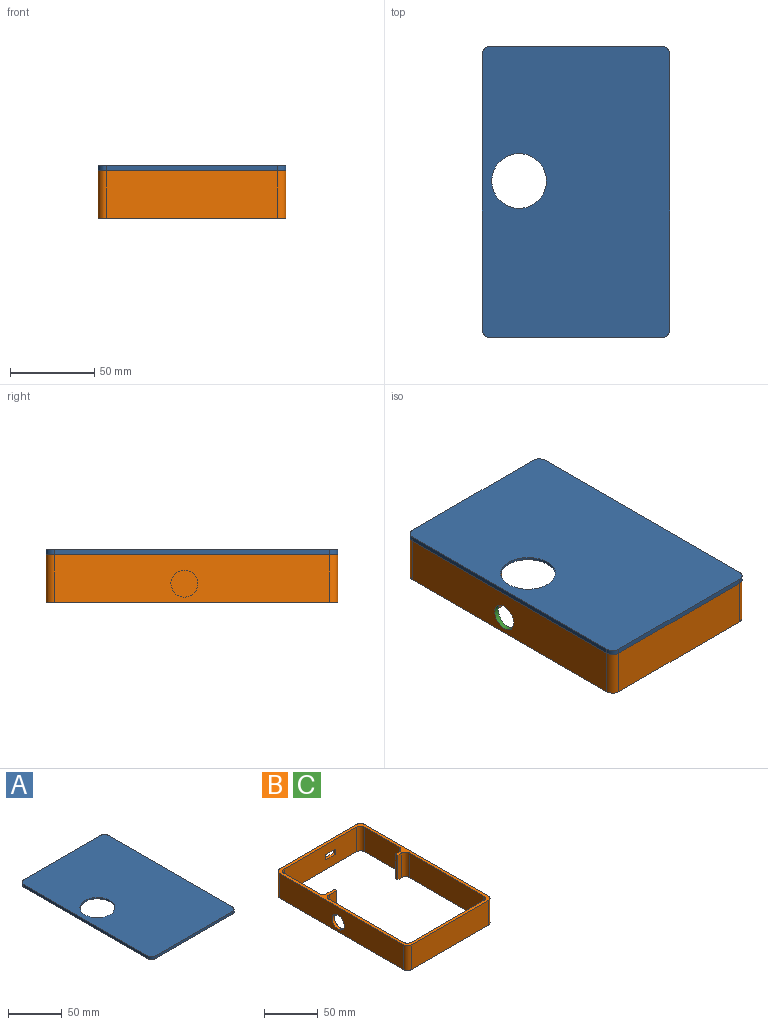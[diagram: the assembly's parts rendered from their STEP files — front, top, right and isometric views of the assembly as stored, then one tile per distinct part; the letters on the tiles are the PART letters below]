
ASSEMBLY  parts=3 mates=1
PART A: 32 faces, bbox 111.5x173x3 mm
  f0: plane 173x111.5mm, normal (0,0,-1), area 1767.5mm2, adj f1,f2,f3,f4,f5,f6,f7,f8
  f1: plane 101.5x3mm, normal (0,1,0), area 304.5mm2, adj f0,f2,f8,f9
  f2: cylinder r=5mm len=5mm, axis (0,0,-1), area 23.6mm2, adj f0,f1,f3,f9
  f3: plane 163x3mm, normal (-1,0,0), area 489mm2, adj f0,f2,f4,f9
  f4: cylinder r=5mm len=5mm, axis (0,0,-1), area 23.6mm2, adj f0,f3,f5,f9
  f5: plane 101.5x3mm, normal (0,-1,0), area 304.5mm2, adj f0,f4,f6,f9
  f6: cylinder r=5mm len=5mm, axis (0,0,-1), area 23.6mm2, adj f0,f5,f7,f9
  f7: plane 163x3mm, normal (1,0,0), area 489mm2, adj f0,f6,f8,f9
  f8: cylinder r=5mm len=5mm, axis (0,0,-1), area 23.6mm2, adj f0,f1,f7,f9
  f9: plane 173x111.5mm, normal (0,0,1), area 18439.7mm2, adj f1,f2,f3,f4,f5,f6,f7,f8
  f10: plane 98x1.5mm, normal (1,0,0), area 147mm2, adj f0,f11,f29,f30
  f11: cylinder r=5mm len=5mm, axis (0,0,-1), area 11.8mm2, adj f0,f10,f12,f30
  f12: plane 95.5x1.5mm, normal (0,1,0), area 143.3mm2, adj f0,f11,f13,f30
  f13: cylinder r=5mm len=5mm, axis (0,0,-1), area 11.8mm2, adj f0,f12,f14,f30
  f14: plane 98x1.5mm, normal (-1,0,0), area 147mm2, adj f0,f13,f15,f30
  f15: cylinder r=5mm len=5mm, axis (0,0,-1), area 11.8mm2, adj f0,f14,f16,f30
  f16: plane 5x1.5mm, normal (0,-1,0), area 7.5mm2, adj f0,f15,f17,f30
  f17: plane 3x1.5mm, normal (-1,0,0), area 4.5mm2, adj f0,f16,f18,f30
  f18: plane 5x1.5mm, normal (0,1,0), area 7.5mm2, adj f0,f17,f19,f30
  f19: cylinder r=5mm len=5mm, axis (0,0,-1), area 11.8mm2, adj f0,f18,f20,f30
  f20: plane 46x1.5mm, normal (-1,0,0), area 69mm2, adj f0,f19,f21,f30
  f21: cylinder r=5mm len=5mm, axis (0,0,-1), area 11.8mm2, adj f0,f20,f22,f30
  f22: plane 95.5x1.5mm, normal (0,-1,0), area 143.3mm2, adj f0,f21,f23,f30
  f23: cylinder r=5mm len=5mm, axis (0,0,-1), area 11.8mm2, adj f0,f22,f24,f30
  f24: plane 46x1.5mm, normal (1,0,0), area 69mm2, adj f0,f23,f25,f30
  f25: cylinder r=5mm len=5mm, axis (0,0,-1), area 11.8mm2, adj f0,f24,f26,f30
  f26: plane 10x1.5mm, normal (0,1,0), area 15mm2, adj f0,f25,f27,f30
  f27: plane 3x1.5mm, normal (1,0,0), area 4.5mm2, adj f0,f26,f28,f30
  f28: plane 10x1.5mm, normal (0,-1,0), area 15mm2, adj f0,f27,f29,f30
  f29: cylinder r=5mm len=5mm, axis (0,0,-1), area 11.8mm2, adj f0,f10,f28,f30
  f30: plane 167x105.5mm, normal (0,0,-1), area 16672.2mm2, adj f10,f11,f12,f13,f14,f15,f16,f17
  f31: cylinder r=16.24mm len=32.48mm, axis (0,0,1), area 153mm2, adj f9,f30
PART B: 35 faces, bbox 111.5x173x28 mm
  f0: plane 101.5x28mm, normal (0,1,0), area 2764mm2, adj f2,f27,f28,f29,f31,f32,f33,f34
  f1: plane 95.5x28mm, normal (0,-1,0), area 2596mm2, adj f19,f20,f28,f29,f31,f32,f33,f34
  f2: cylinder r=5mm len=28mm, axis (0,0,-1), area 219.9mm2, adj f0,f3,f28,f29
  f3: plane 163x28mm, normal (-1,0,0), area 4362.9mm2, adj f2,f4,f28,f29,f30
  f4: cylinder r=5mm len=28mm, axis (0,0,-1), area 219.9mm2, adj f3,f5,f28,f29
  f5: plane 101.5x28mm, normal (0,-1,0), area 2842mm2, adj f4,f6,f28,f29
  f6: cylinder r=5mm len=28mm, axis (0,0,-1), area 219.9mm2, adj f5,f7,f28,f29
  f7: plane 163x28mm, normal (1,0,0), area 4564mm2, adj f6,f27,f28,f29
  f8: plane 98x28mm, normal (-1,0,0), area 2744mm2, adj f9,f26,f28,f29
  f9: cylinder r=5mm len=28mm, axis (0,0,-1), area 219.9mm2, adj f8,f10,f28,f29
  f10: plane 95.5x28mm, normal (0,1,0), area 2674mm2, adj f9,f11,f28,f29
  f11: cylinder r=5mm len=28mm, axis (0,0,-1), area 219.9mm2, adj f10,f12,f28,f29
  f12: plane 98x28mm, normal (1,0,0), area 2542.9mm2, adj f11,f13,f28,f29,f30
  f13: cylinder r=5mm len=28mm, axis (0,0,-1), area 219.9mm2, adj f12,f14,f28,f29
  f14: plane 28x10mm, normal (0,-1,0), area 280mm2, adj f13,f15,f28,f29
  f15: plane 28x3mm, normal (1,0,0), area 84mm2, adj f14,f16,f28,f29
  f16: plane 28x10mm, normal (0,1,0), area 280mm2, adj f15,f17,f28,f29
  f17: cylinder r=5mm len=28mm, axis (0,0,-1), area 219.9mm2, adj f16,f18,f28,f29
  f18: plane 46x28mm, normal (1,0,0), area 1288mm2, adj f17,f19,f28,f29
  f19: cylinder r=5mm len=28mm, axis (0,0,-1), area 219.9mm2, adj f1,f18,f28,f29
  f20: cylinder r=5mm len=28mm, axis (0,0,-1), area 219.9mm2, adj f1,f21,f28,f29
  f21: plane 46x28mm, normal (-1,0,0), area 1288mm2, adj f20,f22,f28,f29
  f22: cylinder r=5mm len=28mm, axis (0,0,-1), area 219.9mm2, adj f21,f23,f28,f29
  f23: plane 28x5mm, normal (0,1,0), area 140mm2, adj f22,f24,f28,f29
  f24: plane 28x3mm, normal (-1,0,0), area 84mm2, adj f23,f25,f28,f29
  f25: plane 28x5mm, normal (0,-1,0), area 140mm2, adj f24,f26,f28,f29
  f26: cylinder r=5mm len=28mm, axis (0,0,-1), area 219.9mm2, adj f8,f25,f28,f29
  f27: cylinder r=5mm len=28mm, axis (0,0,-1), area 219.9mm2, adj f0,f7,f28,f29
  f28: plane 173x111.5mm, normal (0,0,1), area 1767.5mm2, adj f0,f1,f2,f3,f4,f5,f6,f7
  f29: plane 173x111.5mm, normal (0,0,-1), area 1767.5mm2, adj f0,f1,f2,f3,f4,f5,f6,f7
  f30: cylinder r=8mm len=16mm, axis (-1,0,0), area 150.8mm2, adj f3,f12
  f31: plane 6x3mm, normal (-1,0,0), area 18mm2, adj f0,f1,f32,f34
  f32: plane 13x3mm, normal (0,0,1), area 39mm2, adj f0,f1,f31,f33
  f33: plane 6x3mm, normal (1,0,0), area 18mm2, adj f0,f1,f32,f34
  f34: plane 13x3mm, normal (0,0,-1), area 39mm2, adj f0,f1,f31,f33
PART C: same geometry as B
PLACE A t=(52.12,-33.68,55.03)mm
PLACE B t=(5.95,-44.4,27.03)mm
PLACE C t=(5.95,-44.4,27.03)mm
MATE fastened A.f0 <-> B.f28  axis (0,0,-1) through (-5.15,1.74,55.03)mm
